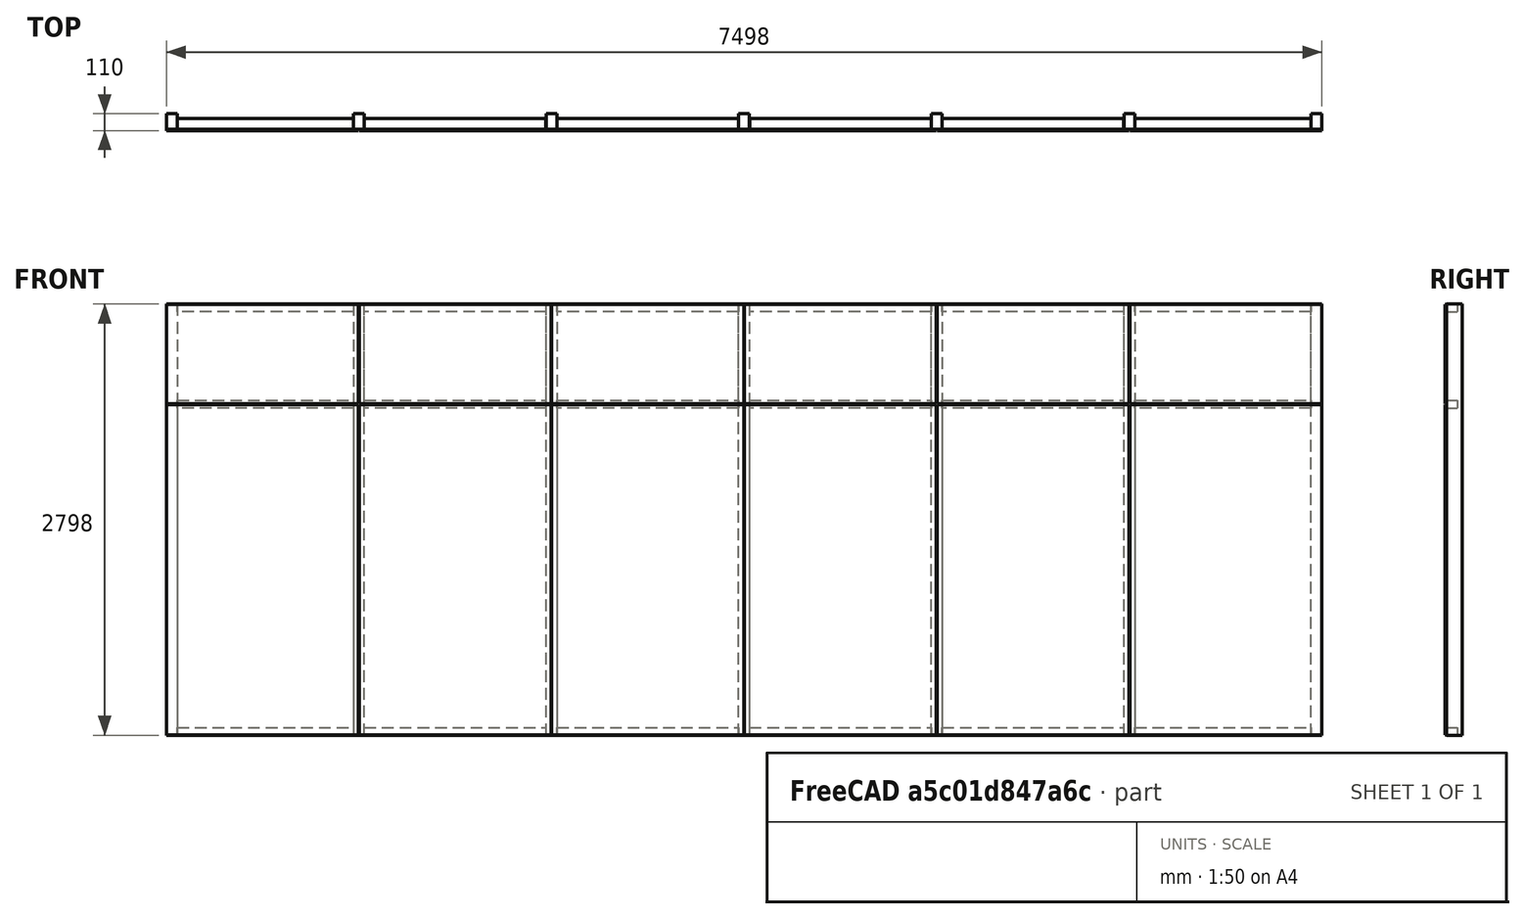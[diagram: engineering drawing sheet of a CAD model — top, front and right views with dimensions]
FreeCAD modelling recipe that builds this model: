
FCSTD DOCUMENT  (FreeCAD 0.16R6704 (Git))
Label: Glass skin 6 fixed modules
License: CreativeCommons Attribution
LicenseURL: http://creativecommons.org/licenses/by/4.0/
objects: Sketcher::SketchObject×1, Part::FeaturePython×1
note: 2 computed .brp shape members not serialized (recipe doc carries the construction recipe); baked Part::Feature solids carry a one-line shape summary decoded from their .brp

FEATURE [Sketcher::SketchObject] Sketch205  label="Esboço pele de vidro "
  Placement = pos=(0,0,0) rot=(1,0,0;1.5708rad)
  sketch-geometry (176):
    g0: LineSegment StartX=0 StartY=0 StartZ=0 EndX=7500 EndY=0 EndZ=0
    g1: LineSegment StartX=7500 StartY=0 StartZ=0 EndX=7500 EndY=2800 EndZ=0
    g2: LineSegment StartX=7500 StartY=2800 StartZ=0 EndX=0 EndY=2800 EndZ=0
    g3: LineSegment StartX=0 StartY=2800 StartZ=0 EndX=0 EndY=0 EndZ=0
    g4: LineSegment StartX=1 StartY=2799 StartZ=0 EndX=71 EndY=2799 EndZ=0
    g5: LineSegment StartX=71 StartY=2799 StartZ=0 EndX=71 EndY=1 EndZ=0
    g6: LineSegment StartX=71 StartY=1 StartZ=0 EndX=1 EndY=1 EndZ=0
    g7: LineSegment StartX=1 StartY=1 StartZ=0 EndX=1 EndY=2799 EndZ=0
    g8: LineSegment StartX=1285 StartY=2799 StartZ=0 EndX=1215 EndY=2799 EndZ=0
    g9: LineSegment StartX=1215 StartY=2799 StartZ=0 EndX=1215 EndY=1 EndZ=0
    g10: LineSegment StartX=1215 StartY=1 StartZ=0 EndX=1285 EndY=1 EndZ=0
    g11: LineSegment StartX=1285 StartY=1 StartZ=0 EndX=1285 EndY=2799 EndZ=0
    g12: LineSegment StartX=72 StartY=2799 StartZ=0 EndX=1214 EndY=2799 EndZ=0
    g13: LineSegment StartX=1214 StartY=2799 StartZ=0 EndX=1214 EndY=2749 EndZ=0
    g14: LineSegment StartX=1214 StartY=2749 StartZ=0 EndX=72 EndY=2749 EndZ=0
    g15: LineSegment StartX=72 StartY=2749 StartZ=0 EndX=72 EndY=2799 EndZ=0
    g16: LineSegment StartX=72 StartY=2175 StartZ=0 EndX=1214 EndY=2175 EndZ=0
    g17: LineSegment StartX=1214 StartY=2175 StartZ=0 EndX=1214 EndY=2125 EndZ=0
    g18: LineSegment StartX=1214 StartY=2125 StartZ=0 EndX=72 EndY=2125 EndZ=0
    g19: LineSegment StartX=72 StartY=2125 StartZ=0 EndX=72 EndY=2175 EndZ=0
    g20: LineSegment StartX=72 StartY=51 StartZ=0 EndX=1214 EndY=51 EndZ=0
    g21: LineSegment StartX=1214 StartY=51 StartZ=0 EndX=1214 EndY=1 EndZ=0
    g22: LineSegment StartX=1214 StartY=1 StartZ=0 EndX=72 EndY=1 EndZ=0
    g23: LineSegment StartX=72 StartY=1 StartZ=0 EndX=72 EndY=51 EndZ=0
    g24: LineSegment [constr] StartX=0 StartY=4045.56 StartZ=0 EndX=0 EndY=0 EndZ=0
    g25: LineSegment [constr] StartX=1250 StartY=4032 StartZ=0 EndX=1250 EndY=-1064.23 EndZ=0
    g26: LineSegment [constr] StartX=2500 StartY=4059.26 StartZ=0 EndX=2500 EndY=-1119 EndZ=0
    g27: LineSegment [constr] StartX=3750 StartY=3908.57 StartZ=0 EndX=3750 EndY=-1023 EndZ=0
    g28: LineSegment [constr] StartX=5000 StartY=3990.77 StartZ=0 EndX=5000 EndY=-934.695 EndZ=0
    g29: LineSegment [constr] StartX=6250 StartY=4286.35 StartZ=0 EndX=6250 EndY=-1160 EndZ=0
    g30: LineSegment [constr] StartX=7500 StartY=4004.47 StartZ=0 EndX=7500 EndY=0 EndZ=0
    g31: LineSegment [constr] StartX=-3381.66 StartY=2150 StartZ=0 EndX=-12333.2 EndY=2150 EndZ=0
    g32: LineSegment [constr] StartX=0 StartY=3388 StartZ=0 EndX=1250 EndY=3388 EndZ=0
    g33: LineSegment [constr] StartX=1250 StartY=3579.79 StartZ=0 EndX=2500 EndY=3579.79 EndZ=0
    g34: LineSegment [constr] StartX=2500 StartY=3223.61 StartZ=0 EndX=3750 EndY=3223.61 EndZ=0
    g35: LineSegment [constr] StartX=3750 StartY=3538.69 StartZ=0 EndX=5000 EndY=3538.69 EndZ=0
    g36: LineSegment [constr] StartX=5000 StartY=3210 StartZ=0 EndX=6250 EndY=3210 EndZ=0
    g37: LineSegment [constr] StartX=6250 StartY=3579.79 StartZ=0 EndX=7500 EndY=3579.79 EndZ=0
    g38: LineSegment [constr] StartX=287.264 StartY=2799 StartZ=0 EndX=287.264 EndY=2749 EndZ=0
    g39: LineSegment [constr] StartX=357.059 StartY=2175 StartZ=0 EndX=357.059 EndY=2125 EndZ=0
    g40: LineSegment [constr] StartX=1 StartY=2367.03 StartZ=0 EndX=71 EndY=2367.03 EndZ=0
    g41: LineSegment [constr] StartX=1215 StartY=2396.22 StartZ=0 EndX=1285 EndY=2396.22 EndZ=0
    g42: LineSegment [constr] StartX=456.696 StartY=51 StartZ=0 EndX=456.696 EndY=1 EndZ=0
    g43: LineSegment StartX=2.5 StartY=2797.5 StartZ=0 EndX=1247.5 EndY=2797.5 EndZ=0
    g44: LineSegment StartX=1247.5 StartY=2797.5 StartZ=0 EndX=1247.5 EndY=2152.5 EndZ=0
    g45: LineSegment StartX=1247.5 StartY=2152.5 StartZ=0 EndX=2.5 EndY=2152.5 EndZ=0
    g46: LineSegment StartX=2.5 StartY=2152.5 StartZ=0 EndX=2.5 EndY=2797.5 EndZ=0
    g47: LineSegment StartX=2465 StartY=2799 StartZ=0 EndX=2535 EndY=2799 EndZ=0
    g48: LineSegment StartX=2535 StartY=2799 StartZ=0 EndX=2535 EndY=1 EndZ=0
    g49: LineSegment StartX=2535 StartY=1 StartZ=0 EndX=2465 EndY=1 EndZ=0
    g50: LineSegment StartX=2465 StartY=1 StartZ=0 EndX=2465 EndY=2799 EndZ=0
    g51: LineSegment StartX=3715 StartY=2799 StartZ=0 EndX=3785 EndY=2799 EndZ=0
    g52: LineSegment StartX=3785 StartY=2799 StartZ=0 EndX=3785 EndY=1 EndZ=0
    g53: LineSegment StartX=3785 StartY=1 StartZ=0 EndX=3715 EndY=1 EndZ=0
    g54: LineSegment StartX=3715 StartY=1 StartZ=0 EndX=3715 EndY=2799 EndZ=0
    g55: LineSegment StartX=4965 StartY=2799 StartZ=0 EndX=5035 EndY=2799 EndZ=0
    g56: LineSegment StartX=5035 StartY=2799 StartZ=0 EndX=5035 EndY=1 EndZ=0
    g57: LineSegment StartX=5035 StartY=1 StartZ=0 EndX=4965 EndY=1 EndZ=0
    g58: LineSegment StartX=4965 StartY=1 StartZ=0 EndX=4965 EndY=2799 EndZ=0
    g59: LineSegment StartX=6215 StartY=2799 StartZ=0 EndX=6285 EndY=2799 EndZ=0
    g60: LineSegment StartX=6285 StartY=2799 StartZ=0 EndX=6285 EndY=1 EndZ=0
    g61: LineSegment StartX=6285 StartY=1 StartZ=0 EndX=6215 EndY=1 EndZ=0
    g62: LineSegment StartX=6215 StartY=1 StartZ=0 EndX=6215 EndY=2799 EndZ=0
    g63: LineSegment StartX=7429 StartY=2799 StartZ=0 EndX=7499 EndY=2799 EndZ=0
    g64: LineSegment StartX=7499 StartY=2799 StartZ=0 EndX=7499 EndY=1 EndZ=0
    g65: LineSegment StartX=7499 StartY=1 StartZ=0 EndX=7429 EndY=1 EndZ=0
    g66: LineSegment StartX=7429 StartY=1 StartZ=0 EndX=7429 EndY=2799 EndZ=0
    g67: LineSegment [constr] StartX=2465 StartY=1674.46 StartZ=0 EndX=2535 EndY=1674.46 EndZ=0
    g68: LineSegment [constr] StartX=3715 StartY=1674.45 StartZ=0 EndX=3785 EndY=1674.45 EndZ=0
    g69: LineSegment [constr] StartX=4965 StartY=1669.74 StartZ=0 EndX=5035 EndY=1669.74 EndZ=0
    g70: LineSegment [constr] StartX=6215 StartY=1602 StartZ=0 EndX=6285 EndY=1602 EndZ=0
    g71: LineSegment [constr] StartX=7429 StartY=1550.78 StartZ=0 EndX=7499 EndY=1550.78 EndZ=0
    g72: LineSegment StartX=1286 StartY=2799 StartZ=0 EndX=2464 EndY=2799 EndZ=0
    g73: LineSegment StartX=2464 StartY=2799 StartZ=0 EndX=2464 EndY=2749 EndZ=0
    g74: LineSegment StartX=2464 StartY=2749 StartZ=0 EndX=1286 EndY=2749 EndZ=0
    g75: LineSegment StartX=1286 StartY=2749 StartZ=0 EndX=1286 EndY=2799 EndZ=0
    g76: LineSegment StartX=1286 StartY=2175 StartZ=0 EndX=2464 EndY=2175 EndZ=0
    g77: LineSegment StartX=2464 StartY=2175 StartZ=0 EndX=2464 EndY=2125 EndZ=0
    g78: LineSegment StartX=2464 StartY=2125 StartZ=0 EndX=1286 EndY=2125 EndZ=0
    g79: LineSegment StartX=1286 StartY=2125 StartZ=0 EndX=1286 EndY=2175 EndZ=0
    g80: LineSegment StartX=1286 StartY=51 StartZ=0 EndX=2464 EndY=51 EndZ=0
    g81: LineSegment StartX=2464 StartY=51 StartZ=0 EndX=2464 EndY=1 EndZ=0
    g82: LineSegment StartX=2464 StartY=1 StartZ=0 EndX=1286 EndY=1 EndZ=0
    g83: LineSegment StartX=1286 StartY=1 StartZ=0 EndX=1286 EndY=51 EndZ=0
    g84: LineSegment StartX=1252.5 StartY=2797.5 StartZ=0 EndX=2497.5 EndY=2797.5 EndZ=0
    g85: LineSegment StartX=2497.5 StartY=2797.5 StartZ=0 EndX=2497.5 EndY=2152.5 EndZ=0
    g86: LineSegment StartX=2497.5 StartY=2152.5 StartZ=0 EndX=1252.5 EndY=2152.5 EndZ=0
    g87: LineSegment StartX=1252.5 StartY=2152.5 StartZ=0 EndX=1252.5 EndY=2797.5 EndZ=0
    g88: LineSegment StartX=2536 StartY=2799 StartZ=0 EndX=3714 EndY=2799 EndZ=0
    g89: LineSegment StartX=3714 StartY=2799 StartZ=0 EndX=3714 EndY=2749 EndZ=0
    g90: LineSegment StartX=3714 StartY=2749 StartZ=0 EndX=2536 EndY=2749 EndZ=0
    g91: LineSegment StartX=2536 StartY=2749 StartZ=0 EndX=2536 EndY=2799 EndZ=0
    g92: LineSegment StartX=2536 StartY=2175 StartZ=0 EndX=3714 EndY=2175 EndZ=0
    g93: LineSegment StartX=3714 StartY=2175 StartZ=0 EndX=3714 EndY=2125 EndZ=0
    g94: LineSegment StartX=3714 StartY=2125 StartZ=0 EndX=2536 EndY=2125 EndZ=0
    g95: LineSegment StartX=2536 StartY=2125 StartZ=0 EndX=2536 EndY=2175 EndZ=0
    g96: LineSegment StartX=2536 StartY=51 StartZ=0 EndX=3714 EndY=51 EndZ=0
    g97: LineSegment StartX=3714 StartY=51 StartZ=0 EndX=3714 EndY=1 EndZ=0
    g98: LineSegment StartX=3714 StartY=1 StartZ=0 EndX=2536 EndY=1 EndZ=0
    g99: LineSegment StartX=2536 StartY=1 StartZ=0 EndX=2536 EndY=51 EndZ=0
    g100: LineSegment StartX=3786 StartY=2799 StartZ=0 EndX=4964 EndY=2799 EndZ=0
    g101: LineSegment StartX=4964 StartY=2799 StartZ=0 EndX=4964 EndY=2749 EndZ=0
    g102: LineSegment StartX=4964 StartY=2749 StartZ=0 EndX=3786 EndY=2749 EndZ=0
    g103: LineSegment StartX=3786 StartY=2749 StartZ=0 EndX=3786 EndY=2799 EndZ=0
    g104: LineSegment StartX=3786 StartY=2175 StartZ=0 EndX=4964 EndY=2175 EndZ=0
    g105: LineSegment StartX=4964 StartY=2175 StartZ=0 EndX=4964 EndY=2125 EndZ=0
    g106: LineSegment StartX=4964 StartY=2125 StartZ=0 EndX=3786 EndY=2125 EndZ=0
    g107: LineSegment StartX=3786 StartY=2125 StartZ=0 EndX=3786 EndY=2175 EndZ=0
    g108: LineSegment StartX=3786 StartY=51 StartZ=0 EndX=4964 EndY=51 EndZ=0
    g109: LineSegment StartX=4964 StartY=51 StartZ=0 EndX=4964 EndY=1 EndZ=0
    g110: LineSegment StartX=4964 StartY=1 StartZ=0 EndX=3786 EndY=1 EndZ=0
    g111: LineSegment StartX=3786 StartY=1 StartZ=0 EndX=3786 EndY=51 EndZ=0
    g112: LineSegment StartX=5036 StartY=2799 StartZ=0 EndX=6214 EndY=2799 EndZ=0
    g113: LineSegment StartX=6214 StartY=2799 StartZ=0 EndX=6214 EndY=2749 EndZ=0
    g114: LineSegment StartX=6214 StartY=2749 StartZ=0 EndX=5036 EndY=2749 EndZ=0
    g115: LineSegment StartX=5036 StartY=2749 StartZ=0 EndX=5036 EndY=2799 EndZ=0
    g116: LineSegment StartX=5036 StartY=2175 StartZ=0 EndX=6214 EndY=2175 EndZ=0
    g117: LineSegment StartX=6214 StartY=2175 StartZ=0 EndX=6214 EndY=2125 EndZ=0
    g118: LineSegment StartX=6214 StartY=2125 StartZ=0 EndX=5036 EndY=2125 EndZ=0
    g119: LineSegment StartX=5036 StartY=2125 StartZ=0 EndX=5036 EndY=2175 EndZ=0
    g120: LineSegment StartX=5036 StartY=51 StartZ=0 EndX=6214 EndY=51 EndZ=0
    g121: LineSegment StartX=6214 StartY=51 StartZ=0 EndX=6214 EndY=1 EndZ=0
    g122: LineSegment StartX=6214 StartY=1 StartZ=0 EndX=5036 EndY=1 EndZ=0
    g123: LineSegment StartX=5036 StartY=1 StartZ=0 EndX=5036 EndY=51 EndZ=0
    g124: LineSegment StartX=6286 StartY=2799 StartZ=0 EndX=7428 EndY=2799 EndZ=0
    g125: LineSegment StartX=7428 StartY=2799 StartZ=0 EndX=7428 EndY=2749 EndZ=0
    g126: LineSegment StartX=7428 StartY=2749 StartZ=0 EndX=6286 EndY=2749 EndZ=0
    g127: LineSegment StartX=6286 StartY=2749 StartZ=0 EndX=6286 EndY=2799 EndZ=0
    g128: LineSegment StartX=6286 StartY=2175 StartZ=0 EndX=7428 EndY=2175 EndZ=0
    g129: LineSegment StartX=7428 StartY=2175 StartZ=0 EndX=7428 EndY=2125 EndZ=0
    g130: LineSegment StartX=7428 StartY=2125 StartZ=0 EndX=6286 EndY=2125 EndZ=0
    g131: LineSegment StartX=6286 StartY=2125 StartZ=0 EndX=6286 EndY=2175 EndZ=0
    g132: LineSegment StartX=6286 StartY=51 StartZ=0 EndX=7428 EndY=51 EndZ=0
    g133: LineSegment StartX=7428 StartY=51 StartZ=0 EndX=7428 EndY=1 EndZ=0
    g134: LineSegment StartX=7428 StartY=1 StartZ=0 EndX=6286 EndY=1 EndZ=0
    g135: LineSegment StartX=6286 StartY=1 StartZ=0 EndX=6286 EndY=51 EndZ=0
    g136: LineSegment StartX=2502.5 StartY=2797.5 StartZ=0 EndX=3747.5 EndY=2797.5 EndZ=0
    g137: LineSegment StartX=3747.5 StartY=2797.5 StartZ=0 EndX=3747.5 EndY=2152.5 EndZ=0
    g138: LineSegment StartX=3747.5 StartY=2152.5 StartZ=0 EndX=2502.5 EndY=2152.5 EndZ=0
    g139: LineSegment StartX=2502.5 StartY=2152.5 StartZ=0 EndX=2502.5 EndY=2797.5 EndZ=0
    g140: LineSegment StartX=3752.5 StartY=2152.5 StartZ=0 EndX=4997.5 EndY=2152.5 EndZ=0
    g141: LineSegment StartX=4997.5 StartY=2152.5 StartZ=0 EndX=4997.5 EndY=2797.5 EndZ=0
    g142: LineSegment StartX=4997.5 StartY=2797.5 StartZ=0 EndX=3752.5 EndY=2797.5 EndZ=0
    g143: LineSegment StartX=3752.5 StartY=2797.5 StartZ=0 EndX=3752.5 EndY=2152.5 EndZ=0
    g144: LineSegment StartX=5002.5 StartY=2797.5 StartZ=0 EndX=6247.5 EndY=2797.5 EndZ=0
    g145: LineSegment StartX=6247.5 StartY=2797.5 StartZ=0 EndX=6247.5 EndY=2152.5 EndZ=0
    g146: LineSegment StartX=6247.5 StartY=2152.5 StartZ=0 EndX=5002.5 EndY=2152.5 EndZ=0
    g147: LineSegment StartX=5002.5 StartY=2152.5 StartZ=0 EndX=5002.5 EndY=2797.5 EndZ=0
    g148: LineSegment StartX=6252.5 StartY=2152.5 StartZ=0 EndX=7497.5 EndY=2152.5 EndZ=0
    g149: LineSegment StartX=7497.5 StartY=2152.5 StartZ=0 EndX=7497.5 EndY=2797.5 EndZ=0
    g150: LineSegment StartX=7497.5 StartY=2797.5 StartZ=0 EndX=6252.5 EndY=2797.5 EndZ=0
    g151: LineSegment StartX=6252.5 StartY=2797.5 StartZ=0 EndX=6252.5 EndY=2152.5 EndZ=0
    g152: LineSegment StartX=2.5 StartY=2147.5 StartZ=0 EndX=1247.5 EndY=2147.5 EndZ=0
    g153: LineSegment StartX=1247.5 StartY=2147.5 StartZ=0 EndX=1247.5 EndY=2.5 EndZ=0
    g154: LineSegment StartX=1247.5 StartY=2.5 StartZ=0 EndX=2.5 EndY=2.5 EndZ=0
    g155: LineSegment StartX=2.5 StartY=2.5 StartZ=0 EndX=2.5 EndY=2147.5 EndZ=0
    g156: LineSegment StartX=1252.5 StartY=2147.5 StartZ=0 EndX=2497.5 EndY=2147.5 EndZ=0
    g157: LineSegment StartX=2497.5 StartY=2147.5 StartZ=0 EndX=2497.5 EndY=2.5 EndZ=0
    g158: LineSegment StartX=2497.5 StartY=2.5 StartZ=0 EndX=1252.5 EndY=2.5 EndZ=0
    g159: LineSegment StartX=1252.5 StartY=2.5 StartZ=0 EndX=1252.5 EndY=2147.5 EndZ=0
    g160: LineSegment StartX=2502.5 StartY=2147.5 StartZ=0 EndX=3747.5 EndY=2147.5 EndZ=0
    g161: LineSegment StartX=3747.5 StartY=2147.5 StartZ=0 EndX=3747.5 EndY=2.5 EndZ=0
    g162: LineSegment StartX=3747.5 StartY=2.5 StartZ=0 EndX=2502.5 EndY=2.5 EndZ=0
    g163: LineSegment StartX=2502.5 StartY=2.5 StartZ=0 EndX=2502.5 EndY=2147.5 EndZ=0
    g164: LineSegment StartX=3752.5 StartY=2147.5 StartZ=0 EndX=4997.5 EndY=2147.5 EndZ=0
    g165: LineSegment StartX=4997.5 StartY=2147.5 StartZ=0 EndX=4997.5 EndY=2.5 EndZ=0
    g166: LineSegment StartX=4997.5 StartY=2.5 StartZ=0 EndX=3752.5 EndY=2.5 EndZ=0
    g167: LineSegment StartX=3752.5 StartY=2.5 StartZ=0 EndX=3752.5 EndY=2147.5 EndZ=0
    g168: LineSegment StartX=5002.5 StartY=2147.5 StartZ=0 EndX=6247.5 EndY=2147.5 EndZ=0
    g169: LineSegment StartX=6247.5 StartY=2147.5 StartZ=0 EndX=6247.5 EndY=2.5 EndZ=0
    g170: LineSegment StartX=6247.5 StartY=2.5 StartZ=0 EndX=5002.5 EndY=2.5 EndZ=0
    g171: LineSegment StartX=5002.5 StartY=2.5 StartZ=0 EndX=5002.5 EndY=2147.5 EndZ=0
    g172: LineSegment StartX=6252.5 StartY=2147.5 StartZ=0 EndX=7497.5 EndY=2147.5 EndZ=0
    g173: LineSegment StartX=7497.5 StartY=2147.5 StartZ=0 EndX=7497.5 EndY=2.5 EndZ=0
    g174: LineSegment StartX=7497.5 StartY=2.5 StartZ=0 EndX=6252.5 EndY=2.5 EndZ=0
    g175: LineSegment StartX=6252.5 StartY=2.5 StartZ=0 EndX=6252.5 EndY=2147.5 EndZ=0
  constraints (513):
    c: Coincident(g0,g1)
    c: Coincident(g1,g2)
    c: Coincident(g2,g3)
    c: Coincident(g3,g0)
    c: Horizontal(g0)
    c: Horizontal(g2)
    c: Vertical(g1)
    c: Vertical(g3)
    c: Coincident(g0,g-1)
    c: DistanceX(g2,g1) = 7500  'Largura do vão'
    c: DistanceY(g-1,g2) = 2800  'Altura do vão'
    c: Coincident(g4,g5)
    c: Coincident(g5,g6)
    c: Coincident(g6,g7)
    c: Coincident(g7,g4)
    c: Horizontal(g4)
    c: Horizontal(g6)
    c: Vertical(g5)
    c: Vertical(g7)
    c: Coincident(g8,g9)
    c: Coincident(g9,g10)
    c: Coincident(g10,g11)
    c: Coincident(g11,g8)
    c: Horizontal(g8)
    c: Horizontal(g10)
    c: Vertical(g9)
    c: Vertical(g11)
    c: Coincident(g12,g13)
    c: Coincident(g13,g14)
    c: Coincident(g14,g15)
    c: Coincident(g15,g12)
    c: Horizontal(g12)
    c: Horizontal(g14)
    c: Vertical(g13)
    c: Vertical(g15)
    c: Coincident(g16,g17)
    c: Coincident(g17,g18)
    c: Coincident(g18,g19)
    c: Coincident(g19,g16)
    c: Horizontal(g16)
    c: Horizontal(g18)
    c: Vertical(g17)
    c: Vertical(g19)
    c: Coincident(g20,g21)
    c: Coincident(g21,g22)
    c: Coincident(g22,g23)
    c: Coincident(g23,g20)
    c: Horizontal(g20)
    c: Horizontal(g22)
    c: Vertical(g21)
    c: Vertical(g23)
    c: Vertical(g24)
    c: Vertical(g30)
    c: PointOnObject(g32,g24)
    c: PointOnObject(g32,g25)
    c: PointOnObject(g33,g25)
    c: PointOnObject(g33,g26)
    c: PointOnObject(g34,g26)
    c: PointOnObject(g34,g27)
    c: PointOnObject(g35,g27)
    c: PointOnObject(g35,g28)
    c: PointOnObject(g36,g28)
    c: PointOnObject(g36,g29)
    c: PointOnObject(g37,g29)
    c: PointOnObject(g37,g30)
    c: Equal(g32,g33)
    c: Equal(g33,g34)
    c: Equal(g34,g35)
    c: Equal(g35,g36)
    c: Equal(g36,g37)
    c: Angle(g32) = 0
    c: Angle(g33) = 0
    c: Angle(g34) = 0
    c: Angle(g35) = 0
    c: Angle(g36) = 0
    c: Angle(g37) = 0
    c: Coincident(g24,g-1)
    c: Coincident(g30,g0)
    c: DistanceY(g-1,g31) = 2150  'Altura da divisão horizontal (eixo)'
    c: Symmetric(g16,g18,g31)  'Constraint85'
    c: Symmetric(g8,g8,g25)  'Constraint84'
    c: DistanceY(g12,g2) = 1  'Constraint83'
    c: DistanceY(g14,g12) = 50  'Altura dos perfis horizontais'
    c: DistanceX(g16,g14) = 0  'Constraint88'
    c: PointOnObject(g38,g12)  'Constraint87'
    c: PointOnObject(g38,g14)  'Constraint86'
    c: PointOnObject(g39,g16)
    c: PointOnObject(g39,g18)
    c: Angle(g38) = -1.5708
    c: Angle(g39) = -1.5708
    c: DistanceX(g2,g4) = 1
    c: DistanceY(g4,g2) = 1
    c: DistanceY(g-1,g6) = 1
    c: DistanceX(g4,g4) = 70  'Largura perfis verticais'
    c: PointOnObject(g40,g7)  'Constraint101'
    c: PointOnObject(g40,g5)
    c: Angle(g40) = 0
    c: DistanceX(g4,g12) = 1
    c: PointOnObject(g41,g9)
    c: PointOnObject(g41,g11)
    c: Angle(g41) = 0
    c: DistanceY(g8,g4) = 0
    c: DistanceY(g5,g9) = 0
    c: PointOnObject(g42,g20)
    c: PointOnObject(g42,g22)
    c: Angle(g42) = -1.5708
    c: DistanceX(g20,g18) = 0
    c: DistanceY(g5,g22) = 0
    c: Equal(g38,g39)
    c: Equal(g39,g42)
    c: DistanceX(g12,g8) = 1
    c: DistanceX(g13,g16) = 0
    c: DistanceX(g17,g20) = 0
    c: Coincident(g43,g44)
    c: Coincident(g44,g45)
    c: Coincident(g45,g46)
    c: Coincident(g46,g43)
    c: Horizontal(g43)
    c: Horizontal(g45)
    c: Vertical(g44)
    c: Vertical(g46)
    c: DistanceY(g43,g4) = 1.5
    c: DistanceX(g4,g43) = 1.5
    c: Coincident(g47,g48)
    c: Coincident(g48,g49)
    c: Coincident(g49,g50)
    c: Coincident(g50,g47)
    c: Horizontal(g47)
    c: Horizontal(g49)
    c: Vertical(g48)
    c: Vertical(g50)
    c: Coincident(g51,g52)
    c: Coincident(g52,g53)
    c: Coincident(g53,g54)
    c: Coincident(g54,g51)
    c: Horizontal(g51)
    c: Horizontal(g53)
    c: Vertical(g52)
    c: Vertical(g54)
    c: Coincident(g55,g56)
    c: Coincident(g56,g57)
    c: Coincident(g57,g58)
    c: Coincident(g58,g55)
    c: Horizontal(g55)
    c: Horizontal(g57)
    c: Vertical(g56)
    c: Vertical(g58)
    c: Coincident(g59,g60)
    c: Coincident(g60,g61)
    c: Coincident(g61,g62)
    c: Coincident(g62,g59)
    c: Horizontal(g59)
    c: Horizontal(g61)
    c: Vertical(g60)
    c: Vertical(g62)
    c: Coincident(g63,g64)
    c: Coincident(g64,g65)
    c: Coincident(g65,g66)
    c: Coincident(g66,g63)
    c: Horizontal(g63)
    c: Horizontal(g65)
    c: Vertical(g64)
    c: Vertical(g66)
    c: DistanceY(g47,g8) = 0
    c: Symmetric(g47,g47,g26)
    c: DistanceY(g51,g47) = 0
    c: Symmetric(g51,g51,g27)
    c: DistanceY(g55,g51) = 0
    c: Symmetric(g55,g55,g28)
    c: DistanceY(g55,g59) = 0
    c: Symmetric(g59,g59,g29)
    c: DistanceY(g63,g59) = 0
    c: DistanceX(g63,g1) = 1
    c: DistanceY(g10,g49) = 0
    c: DistanceY(g48,g53) = 0
    c: DistanceY(g52,g57) = 0
    c: DistanceY(g56,g61) = 0
    c: DistanceY(g60,g65) = 0
    c: PointOnObject(g67,g50)
    c: PointOnObject(g67,g48)
    c: PointOnObject(g68,g54)
    c: PointOnObject(g68,g52)
    c: PointOnObject(g69,g58)
    c: PointOnObject(g69,g56)
    c: PointOnObject(g70,g62)
    c: PointOnObject(g70,g60)
    c: PointOnObject(g71,g66)
    c: PointOnObject(g71,g64)
    c: Angle(g71) = 0
    c: Angle(g70) = 0
    c: Angle(g69) = 0
    c: Angle(g68) = 0
    c: Angle(g67) = 0
    c: Equal(g40,g41)
    c: Equal(g41,g67)
    c: Equal(g67,g68)
    c: Equal(g68,g69)
    c: Equal(g69,g70)
    c: Equal(g70,g71)
    c: Coincident(g72,g73)
    c: Coincident(g73,g74)
    c: Coincident(g74,g75)
    c: Coincident(g75,g72)
    c: Horizontal(g72)
    c: Horizontal(g74)
    c: Vertical(g73)
    c: Vertical(g75)
    c: Coincident(g76,g77)
    c: Coincident(g77,g78)
    c: Coincident(g78,g79)
    c: Coincident(g79,g76)
    c: Horizontal(g76)
    c: Horizontal(g78)
    c: Vertical(g77)
    c: Vertical(g79)
    c: Coincident(g80,g81)
    c: Coincident(g81,g82)
    c: Coincident(g82,g83)
    c: Coincident(g83,g80)
    c: Horizontal(g80)
    c: Horizontal(g82)
    c: Vertical(g81)
    c: Vertical(g83)
    c: DistanceX(g8,g72) = 1
    c: DistanceY(g72,g12) = 0
    c: DistanceY(g74,g13) = 0
    c: DistanceX(g74,g76) = 0
    c: DistanceY(g16,g76) = 0
    c: DistanceY(g78,g17) = 0
    c: DistanceX(g78,g80) = 0
    c: DistanceY(g21,g82) = 0
    c: DistanceY(g20,g80) = 0
    c: DistanceX(g72,g47) = 1
    c: DistanceX(g76,g73) = 0
    c: DistanceX(g80,g77) = 0
    c: Coincident(g84,g85)
    c: Coincident(g85,g86)
    c: Coincident(g86,g87)
    c: Coincident(g87,g84)
    c: Horizontal(g84)
    c: Horizontal(g86)
    c: Vertical(g85)
    c: Vertical(g87)
    c: DistanceY(g84,g43) = 0
    c: DistanceY(g44,g86) = 0
    c: Symmetric(g44,g86,g25)
    c: DistanceX(g44,g86) = 5
    c: Coincident(g88,g89)
    c: Coincident(g89,g90)
    c: Coincident(g90,g91)
    c: Coincident(g91,g88)
    c: Horizontal(g88)
    c: Horizontal(g90)
    c: Vertical(g89)
    c: Vertical(g91)
    c: Coincident(g92,g93)
    c: Coincident(g93,g94)
    c: Coincident(g94,g95)
    c: Coincident(g95,g92)
    c: Horizontal(g92)
    c: Horizontal(g94)
    c: Vertical(g93)
    c: Vertical(g95)
    c: Coincident(g96,g97)
    c: Coincident(g97,g98)
    c: Coincident(g98,g99)
    c: Coincident(g99,g96)
    c: Horizontal(g96)
    c: Horizontal(g98)
    c: Vertical(g97)
    c: Vertical(g99)
    c: Coincident(g100,g101)
    c: Coincident(g101,g102)
    c: Coincident(g102,g103)
    c: Coincident(g103,g100)
    c: Horizontal(g100)
    c: Horizontal(g102)
    c: Vertical(g101)
    c: Vertical(g103)
    c: Coincident(g104,g105)
    c: Coincident(g105,g106)
    c: Coincident(g106,g107)
    c: Coincident(g107,g104)
    c: Horizontal(g104)
    c: Horizontal(g106)
    c: Vertical(g105)
    c: Vertical(g107)
    c: Coincident(g108,g109)
    c: Coincident(g109,g110)
    c: Coincident(g110,g111)
    c: Coincident(g111,g108)
    c: Horizontal(g108)
    c: Horizontal(g110)
    c: Vertical(g109)
    c: Vertical(g111)
    c: Coincident(g112,g113)
    c: Coincident(g113,g114)
    c: Coincident(g114,g115)
    c: Coincident(g115,g112)
    c: Horizontal(g112)
    c: Horizontal(g114)
    c: Vertical(g113)
    c: Vertical(g115)
    c: Coincident(g116,g117)
    c: Coincident(g117,g118)
    c: Coincident(g118,g119)
    c: Coincident(g119,g116)
    c: Horizontal(g116)
    c: Horizontal(g118)
    c: Vertical(g117)
    c: Vertical(g119)
    c: Coincident(g120,g121)
    c: Coincident(g121,g122)
    c: Coincident(g122,g123)
    c: Coincident(g123,g120)
    c: Horizontal(g120)
    c: Horizontal(g122)
    c: Vertical(g121)
    c: Vertical(g123)
    c: Coincident(g124,g125)
    c: Coincident(g125,g126)
    c: Coincident(g126,g127)
    c: Coincident(g127,g124)
    c: Horizontal(g124)
    c: Horizontal(g126)
    c: Vertical(g125)
    c: Vertical(g127)
    c: Coincident(g128,g129)
    c: Coincident(g129,g130)
    c: Coincident(g130,g131)
    c: Coincident(g131,g128)
    c: Horizontal(g128)
    c: Horizontal(g130)
    c: Vertical(g129)
    c: Vertical(g131)
    c: Coincident(g132,g133)
    c: Coincident(g133,g134)
    c: Coincident(g134,g135)
    c: Coincident(g135,g132)
    c: Horizontal(g132)
    c: Horizontal(g134)
    c: Vertical(g133)
    c: Vertical(g135)
    c: DistanceX(g47,g88) = 1
    c: DistanceY(g88,g72) = 0
    c: DistanceY(g90,g73) = 0
    c: DistanceX(g90,g92) = 0
    c: DistanceY(g76,g92) = 0
    c: DistanceY(g94,g77) = 0
    c: DistanceX(g94,g96) = 0
    c: DistanceY(g80,g96) = 0
    c: DistanceY(g81,g98) = 0
    c: DistanceX(g88,g51) = 1
    c: DistanceX(g92,g89) = 0
    c: DistanceX(g96,g93) = 0
    c: DistanceX(g51,g100) = 1
    c: DistanceY(g100,g88) = 0
    c: DistanceY(g102,g89) = 0
    c: DistanceX(g102,g104) = 0
    c: DistanceY(g92,g104) = 0
    c: DistanceY(g106,g93) = 0
    c: DistanceX(g106,g108) = 0
    c: DistanceY(g96,g108) = 0
    c: DistanceY(g97,g110) = 0
    c: DistanceX(g100,g55) = 1
    c: DistanceX(g104,g101) = 0
    c: DistanceX(g108,g105) = 0
    c: DistanceX(g55,g112) = 1
    c: DistanceY(g112,g100) = 0
    c: DistanceY(g114,g101) = 0
    c: DistanceX(g114,g116) = 0
    c: DistanceY(g104,g116) = 0
    c: DistanceY(g118,g105) = 0
    c: DistanceX(g118,g120) = 0
    c: DistanceY(g108,g120) = 0
    c: DistanceY(g122,g109) = 0
    c: DistanceX(g112,g59) = 1
    c: DistanceX(g116,g113) = 0
    c: DistanceX(g120,g117) = 0
    c: DistanceX(g59,g124) = 1
    c: DistanceY(g124,g112) = 0
    c: DistanceY(g126,g113) = 0
    c: DistanceX(g126,g128) = 0
    c: DistanceY(g116,g128) = 0
    c: DistanceY(g130,g117) = 0
    c: DistanceX(g130,g132) = 0
    c: DistanceY(g120,g132) = 0
    c: DistanceY(g121,g134) = 0
    c: DistanceX(g124,g63) = 1
    c: DistanceX(g128,g125) = 0
    c: DistanceX(g132,g129) = 0
    c: Coincident(g136,g137)
    c: Coincident(g137,g138)
    c: Coincident(g138,g139)
    c: Coincident(g139,g136)
    c: Horizontal(g136)
    c: Horizontal(g138)
    c: Vertical(g137)
    c: Vertical(g139)
    c: Coincident(g140,g141)
    c: Coincident(g141,g142)
    c: Coincident(g142,g143)
    c: Coincident(g143,g140)
    c: Horizontal(g140)
    c: Horizontal(g142)
    c: Vertical(g141)
    c: Vertical(g143)
    c: Coincident(g144,g145)
    c: Coincident(g145,g146)
    c: Coincident(g146,g147)
    c: Coincident(g147,g144)
    c: Horizontal(g144)
    c: Horizontal(g146)
    c: Vertical(g145)
    c: Vertical(g147)
    c: Coincident(g148,g149)
    c: Coincident(g149,g150)
    c: Coincident(g150,g151)
    c: Coincident(g151,g148)
    c: Horizontal(g148)
    c: Horizontal(g150)
    c: Vertical(g149)
    c: Vertical(g151)
    c: DistanceY(g136,g84) = 0
    c: DistanceX(g84,g136) = 5
    c: Symmetric(g84,g136,g26)
    c: DistanceY(g85,g138) = 0
    c: DistanceY(g142,g136) = 0
    c: Symmetric(g136,g142,g27)
    c: DistanceX(g136,g142) = 5
    c: DistanceY(g137,g140) = 0
    c: DistanceY(g144,g141) = 0
    c: Symmetric(g141,g144,g28)
    c: DistanceX(g141,g144) = 5
    c: DistanceY(g140,g146) = 0
    c: DistanceY(g150,g144) = 0
    c: Symmetric(g144,g150,g29)
    c: DistanceX(g144,g150) = 5
    c: DistanceY(g145,g148) = 0
    c: DistanceX(g149,g63) = 1.5
    c: Coincident(g152,g153)
    c: Coincident(g153,g154)
    c: Coincident(g154,g155)
    c: Coincident(g155,g152)
    c: Horizontal(g152)
    c: Horizontal(g154)
    c: Vertical(g153)
    c: Vertical(g155)
    c: Coincident(g156,g157)
    c: Coincident(g157,g158)
    c: Coincident(g158,g159)
    c: Coincident(g159,g156)
    c: Horizontal(g156)
    c: Horizontal(g158)
    c: Vertical(g157)
    c: Vertical(g159)
    c: Coincident(g160,g161)
    c: Coincident(g161,g162)
    c: Coincident(g162,g163)
    c: Coincident(g163,g160)
    c: Horizontal(g160)
    c: Horizontal(g162)
    c: Vertical(g161)
    c: Vertical(g163)
    c: Coincident(g164,g165)
    c: Coincident(g165,g166)
    c: Coincident(g166,g167)
    c: Coincident(g167,g164)
    c: Horizontal(g164)
    c: Horizontal(g166)
    c: Vertical(g165)
    c: Vertical(g167)
    c: Coincident(g168,g169)
    c: Coincident(g169,g170)
    c: Coincident(g170,g171)
    c: Coincident(g171,g168)
    c: Horizontal(g168)
    c: Horizontal(g170)
    c: Vertical(g169)
    c: Vertical(g171)
    c: Coincident(g172,g173)
    c: Coincident(g173,g174)
    c: Coincident(g174,g175)
    c: Coincident(g175,g172)
    c: Horizontal(g172)
    c: Horizontal(g174)
    c: Vertical(g173)
    c: Vertical(g175)
    c: DistanceX(g45,g152) = 0
    c: Symmetric(g152,g45,g31)
    c: DistanceY(g152,g45) = 5
    c: DistanceY(g6,g154) = 1.5
    c: DistanceX(g152,g44) = 0
    c: DistanceX(g86,g156) = 0
    c: DistanceY(g156,g152) = 0
    c: DistanceY(g153,g158) = 0
    c: DistanceX(g156,g85) = 0
    c: DistanceY(g160,g156) = 0
    c: DistanceX(g138,g160) = 0
    c: DistanceY(g157,g162) = 0
    c: DistanceX(g160,g137) = 0
    c: DistanceY(g164,g160) = 0
    c: DistanceX(g140,g164) = 0
    c: DistanceY(g161,g166) = 0
    c: DistanceX(g164,g140) = 0
    c: DistanceY(g168,g164) = 0
    c: DistanceX(g146,g168) = 0
    c: DistanceY(g165,g170) = 0
    c: DistanceX(g168,g145) = 0
    c: DistanceY(g172,g168) = 0
    c: DistanceX(g148,g172) = 0
    c: DistanceX(g172,g148) = 0
    c: DistanceY(g169,g174) = 0
FEATURE [Part::FeaturePython] Window121  label="Glass skin 6 fixed modules"  # WARN: FeaturePython — macro-defined, semantics opaque (R4)
  Base = -> Sketch205
  Height = 0
  HoleDepth = 0
  MoveWithHost = true
  Normal = (0,1,0)
  Preset = 0
  Role = 0
  Width = 0
  WindowParts = MONTANTE VERTICAL 1 | Frame | Wire1 | 100.0 | 0.0 | MONTANTE VERTICAL 2 | Frame | Wire2 | 100.0 | 0.0 | MONTANTE VERTICAL 3 | Frame | Wire7 | 100.0 | 0.0 | MONTANTE VERTICAL 4 | Frame | Wire8 | 100.0 | 0.0 | MONTANTE VERTICAL 5 | Frame | Wire9 | 100.0 | 0.0 | MONTANTE VERTICAL 6 | Frame | Wire10 | 100.0 | 0.0 | MONTANTE VERTICAL 7 | Frame | Wire11 | 100.0 | 0.0 | MONTANTE HORIZONTAL 1 | Frame | Wire3 | 70.0 | 0.0 | MONTANTE HORIZONTAL 2 | Frame | Wire4 | 70.0 | 0.0 | MONTANTE HORIZONTAL 3 | Frame | Wire5 | 70.0 | 0.0 | MONTANTE HORIZONTAL 4 | Frame | Wire12 | 70.0 | 0.0 | MONTANTE HORIZONTAL 5 | Frame | Wire13 | 70.0 | 0.0 | MONTANTE HORIZONTAL 6 | Frame | Wire14 | 70.0 | 0.0 | MONTANTE HORIZONTAL 7 | Frame | Wire16 | 70.0 | 0.0 | MONTANTE HORIZONTAL 8 | Frame | Wire17 | 70.0 | 0.0 | MONTANTE HORIZONTAL 9 | Frame | Wire18 | 70.0 | 0.0 | MONTANTE HORIZONTAL 10 | Frame | Wire19 | 70.0 | 0.0 | MONTANTE HORIZONTAL 11 | Frame | Wire20 | 70.0 | 0.0 | MONTANTE HORIZONTAL 12 | Frame | Wire21 | 70.0 | 0.0 | MONTANTE HORIZONTAL 13 | Frame | Wire22 | 70.0 | 0.0 | MONTANTE HORIZONTAL 14 | Frame | Wire23 | 70.0 | 0.0 | MONTANTE HORIZONTAL 15 | Frame | Wire24 | 70.0 | 0.0 | MONTANTE HORIZONTAL 16 | Frame | Wire25 | 70.0 | 0.0 | MONTANTE HORIZONTAL 17 | Frame | Wire26 | 70.0 | 0.0 | MONTANTE HORIZONTAL 18 | Frame | Wire27 | 70.0 | 0.0 | VIDRO 1 | Glass panel | Wire6 | 10.0 | -10.0 | VIDRO 2 | Glass panel | Wire15 | 10.0 | -10.0 | VIDRO 3 | Glass panel | Wire28 | 10.0 | -10.0 | VIDRO 4 | Glass panel | Wire29 | 10.0 | -10.0 | VIDRO 5 | Glass panel | Wire30 | 10.0 | -10.0 | VIDRO 6 | Glass panel | Wire31 | 10.0 | -10.0 | VIDRO 7 | Glass panel | Wire32 | 10.0 | -10.0 | VIDRO 8 | Glass panel | Wire33 | 10.0 | -10.0 | VIDRO 9 | Glass panel | Wire34 | 10.0 | -10.0 | VIDRO 10 | Glass panel | Wire35 | 10.0 | -10.0 | VIDRO 11 | Glass panel | Wire36 | 10.0 | -10.0 | VIDRO 12 | Glass panel | Wire37 | 10.0 | -10.0
